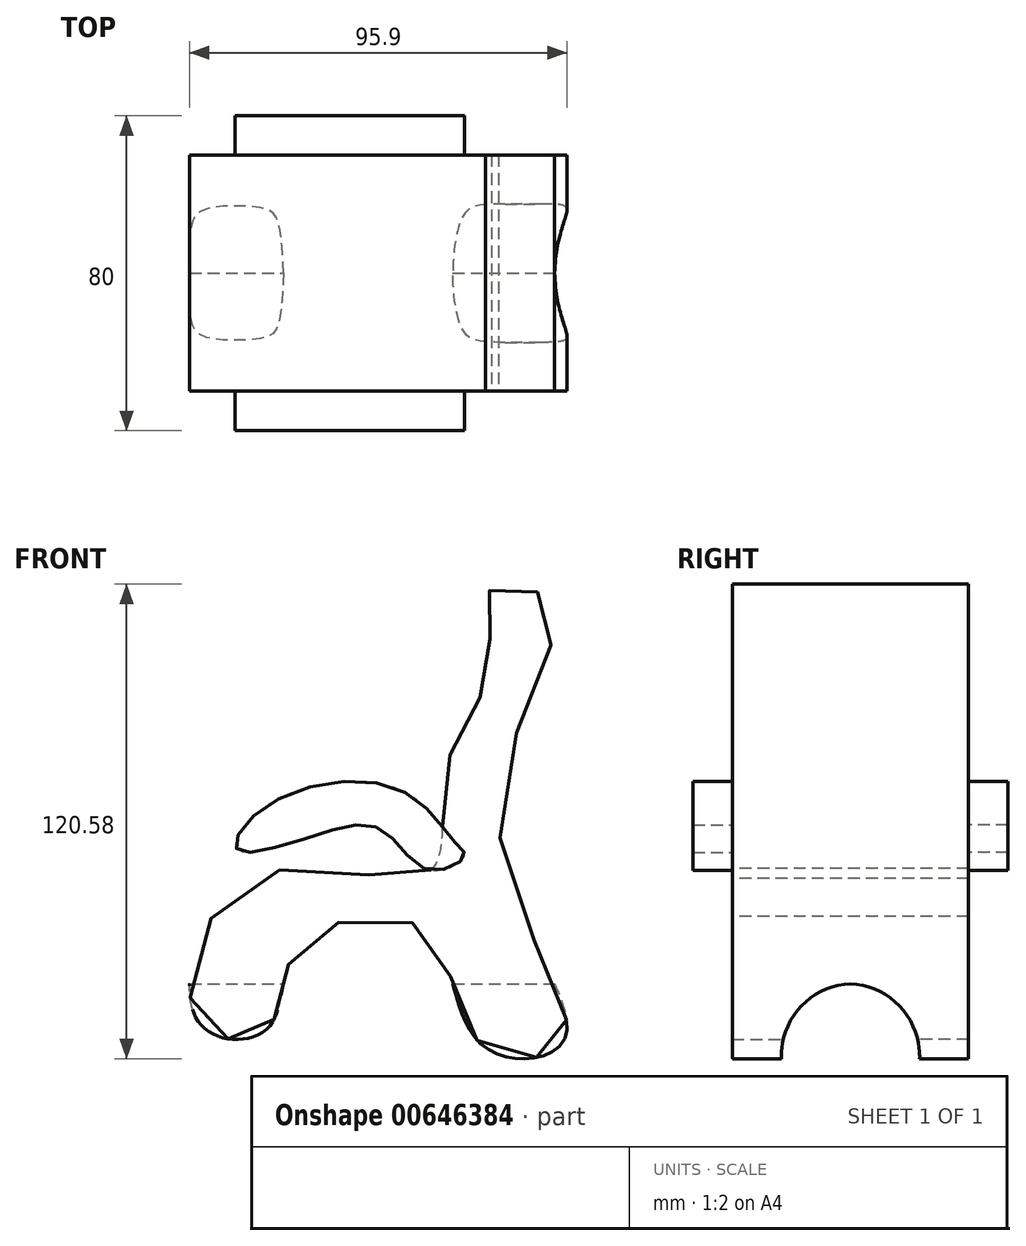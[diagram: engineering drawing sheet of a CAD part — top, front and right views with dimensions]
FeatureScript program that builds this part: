
annotation { "Feature Type Name" : "Feature", "Feature Type Description" : "" }
export const myFeature = defineFeature(function(context is Context, id is Id, definition is map)
    precondition{}
    {
        {
            var Q0;
            Q0=qCreatedBy(makeId("Front.planeOp"),FACE);
            var sketch = newSketch(context, id + "F0", { "sketchPlane" : qUnion([Q0])});
            skFitSpline(sketch, "E0", {"points": [v(-8.84, 44.93) * mm, v(-8.63, 26.07) * mm, v(-20.02, 0) * mm, v(-24.94, -27.23) * mm, v(-68.63, -28.2) * mm, v(-83.26, -64.65) * mm, v(-65.55, -66.7) * mm, v(-57.6, -45.91) * mm, v(-25.52, -41.8) * mm, v(-11.15, -70.8) * mm, v(9.9, -69.52) * mm, v(-6.79, -14.35) * mm, v(6.56, 40.56) * mm, v(-8.84, 44.93) * mm]});
            skSolve(sketch);
        }
        {
            var Q0;
            Q0=makeQuery(id+"F0.imprint","IMPRINT",FACE,{"disambiguationData":[TD([[makeQuery(id+"F0.imprint","IMPRINT",EDGE,{"derivedFrom":sQuery(id+"F0.wireOp",EDGE,"E0")}),1.0]])]});
            extrude(context, id + "F1", {"entities" : qUnion([Q0]), "depth" : 60 * mm, "offsetDistance" : 25 * mm});
        }
        {
            var Q0;
            Q0=qCreatedBy(makeId("Right.planeOp"),FACE);
            var sketch = newSketch(context, id + "F2", { "sketchPlane" : qUnion([Q0])});
            skCircle(sketch, "E1", {"center": v(-30.92, -73.78) * mm, "radius": 18.51 * mm});
            skSolve(sketch);
        }
        {
            var Q0;
            Q0=makeQuery(id+"F2.imprint","IMPRINT",FACE,{"disambiguationData":[TD([[makeQuery(id+"F2.imprint","IMPRINT",EDGE,{"derivedFrom":sQuery(id+"F2.wireOp",EDGE,"E1")}),1.0]])]});
            extrude(context, id + "F3", {"entities" : qUnion([Q0]), "operationType" : NewBodyOperationType.REMOVE, "oppositeDirection" : true, "depth" : 101 * mm, "offsetDistance" : 25 * mm});
        }
        {
            var Q0;
            Q0=makeQuery(id+"F3.boolean.opBoolean","COPY",FACE,{"derivedFrom":makeQuery(id+"F3.opExtrude","CAP_FACE",FACE,{"disambiguationData":[OSD([sQuery(id+"F2.wireOp",EDGE,"E1")])],"isStart":true})});
            extrude(context, id + "F4", {"entities" : qUnion([Q0]), "operationType" : NewBodyOperationType.REMOVE, "oppositeDirection" : true, "depth" : 25 * mm, "offsetDistance" : 25 * mm});
        }
        {
            var Q0;
            Q0=qCreatedBy(makeId("Front.planeOp"),FACE);
            var sketch = newSketch(context, id + "F5", { "sketchPlane" : qUnion([Q0])});
            skFitSpline(sketch, "E2", {"points": [v(-17.83, -19.37) * mm, v(-31.95, -6.03) * mm, v(-65.82, -10.14) * mm, v(-73.26, -21.17) * mm, v(-53.25, -17.58) * mm, v(-36.31, -16.3) * mm, v(-24.76, -26.3) * mm, v(-15.52, -22.97) * mm, v(-17.83, -19.37) * mm]});
            skSolve(sketch);
        }
        {
            var Q0;
            Q0=makeQuery(id+"F5.imprint","IMPRINT",FACE,{"disambiguationData":[TD([[makeQuery(id+"F5.imprint","IMPRINT",EDGE,{"derivedFrom":sQuery(id+"F5.wireOp",EDGE,"E2")}),1.0]])]});
            extrude(context, id + "F6", {"entities" : qUnion([Q0]), "operationType" : NewBodyOperationType.ADD, "oppositeDirection" : true, "depth" : 10 * mm, "offsetDistance" : 25 * mm});
        }
        {
            var Q0;
            Q0=qCreatedBy(makeId("Front.planeOp"),FACE);
            cPlane(context, id + "F7", {"entities" : qUnion([Q0]), "cplaneType" : CPlaneType.OFFSET, "offset" : 30 * mm, "width" : 150 * mm, "height" : 150 * mm});
        }
        {
            var Q0;
            Q0=makeQuery(id+"F1.opExtrude","SWEPT_BODY",BODY,{"disambiguationData":[OSD([sQuery(id+"F0.wireOp",EDGE,"E0")])]});
            var Q1;
            Q1=qCreatedBy(id+"F7.planeOp",FACE);
            mirror(context, id + "F8", {"operationType" : NewBodyOperationType.ADD, "entities" : qUnion([Q0]), "mirrorPlane" : qUnion([Q1])});
        }
    });
